# Revit family: Glulam-Southern Pine-Column
name_source: partatom
category: Structural Columns
revit_build: Autodesk Revit Architecture 2012 (Build: 20110210_1515)
units: mm (PartAtom-declared; Revit-internal decimal feet)

## types (160) — shared parameters
Assembly Code = B10

## per-type parameters (varying)
| type | A | Ix | Iy | Laminations | Sx | Sy | b | d |
| 3x5.5 | 16.5 in² | 41.59 | 12.38 | 4 | 15.13 | 8.25 | 0' - 3" | 0' - 5 1/2" |
| 3x6.875 | 20.63 in² | 81.24 | 15.47 | 5 | 23.63 | 10.31 | 0' - 3" | 0' - 6 7/8" |
| 3x8.25 | 24.75 in² | 140.4 | 18.56 | 6 | 34.03 | 12.38 | 0' - 3" | 0' - 8 1/4" |
| 3x9.625 | 28.88 in² | 222.9 | 21.66 | 7 | 46.32 | 14.44 | 0' - 3" | 0' - 9 5/8" |
| 3x11 | 33 in² | 332.8 | 24.75 | 8 | 60.5 | 16.5 | 0' - 3" | 0' - 11" |
| 3x12.375 | 37.13 in² | 473.8 | 27.84 | 9 | 76.57 | 18.56 | 0' - 3" | 1' - 0 3/8" |
| 3x13.75 | 41.25 in² | 649.9 | 30.94 | 10 | 94.53 | 20.63 | 0' - 3" | 1' - 1 3/4" |
| 3x15.125 | 45.38 in² | 865 | 34.03 | 11 | 114.4 | 22.69 | 0' - 3" | 1' - 3 1/8" |
| 3x16.5 | 49.5 in² | 1123 | 37.13 | 12 | 136.1 | 24.75 | 0' - 3" | 1' - 4 1/2" |
| 3x17.875 | 53.63 in² | 1428 | 40.22 | 13 | 159.8 | 26.81 | 0' - 3" | 1' - 5 7/8" |
| 3x19.25 | 57.75 in² | 1783 | 43.31 | 14 | 185.3 | 28.88 | 0' - 3" | 1' - 7 1/4" |
| 3x20.625 | 61.88 in² | 2193 | 46.41 | 15 | 212.7 | 30.94 | 0' - 3" | 1' - 8 5/8" |
| 3x22 | 66 in² | 2662 | 49.5 | 16 | 242 | 33 | 0' - 3" | 1' - 10" |
| 3x23.375 | 70.13 in² | 3193 | 52.59 | 17 | 273.2 | 35.06 | 0' - 3" | 1' - 11 3/8" |
| 3x24.75 | 74.25 in² | 3790 | 55.69 | 18 | 306.3 | 37.13 | 0' - 3" | 2' - 0 3/4" |
| 5x5.5 | 27.5 in² | 69.32 | 57.29 | 4 | 25.21 | 22.92 | 0' - 5" | 0' - 5 1/2" |
| 5x6.875 | 34.38 in² | 135.4 | 71.61 | 5 | 39.39 | 28.65 | 0' - 5" | 0' - 6 7/8" |
| 5x8.25 | 41.25 in² | 234 | 85.94 | 6 | 56.72 | 34.38 | 0' - 5" | 0' - 8 1/4" |
| 5x9.625 | 48.13 in² | 371.5 | 100.3 | 7 | 77.2 | 40.1 | 0' - 5" | 0' - 9 5/8" |
| 5x11 | 55 in² | 554.6 | 114.6 | 8 | 100.8 | 45.83 | 0' - 5" | 0' - 11" |
| 5x12.375 | 61.88 in² | 789.6 | 128.9 | 9 | 127.6 | 51.56 | 0' - 5" | 1' - 0 3/8" |
| 5x13.75 | 68.75 in² | 1083 | 143.2 | 10 | 157.6 | 57.29 | 0' - 5" | 1' - 1 3/4" |
| 5x15.125 | 75.63 in² | 1442 | 157.6 | 11 | 190.6 | 63.02 | 0' - 5" | 1' - 3 1/8" |
| 5x16.5 | 82.5 in² | 1872 | 171.9 | 12 | 226.9 | 68.75 | 0' - 5" | 1' - 4 1/2" |
| 5x17.875 | 89.38 in² | 2380 | 186.2 | 13 | 266.3 | 74.48 | 0' - 5" | 1' - 5 7/8" |
| 5x19.25 | 96.25 in² | 2972 | 200.5 | 14 | 308.8 | 80.21 | 0' - 5" | 1' - 7 1/4" |
| 5x20.625 | 103.1 in² | 3656 | 214.8 | 15 | 354.5 | 85.94 | 0' - 5" | 1' - 8 5/8" |
| 5x22 | 110 in² | 4437 | 229.2 | 16 | 403.3 | 91.67 | 0' - 5" | 1' - 10" |
| 5x23.375 | 116.9 in² | 5322 | 243.5 | 17 | 455.3 | 97.4 | 0' - 5" | 1' - 11 3/8" |
| 5x24.75 | 123.8 in² | 6317 | 257.8 | 18 | 510.5 | 103.1 | 0' - 5" | 2' - 0 3/4" |
| 5x26.125 | 130.6 in² | 7429 | 272.1 | 19 | 568.8 | 108.9 | 0' - 5" | 2' - 2 1/8" |
| 5x27.5 | 137.5 in² | 8665 | 286.5 | 20 | 630.2 | 114.6 | 0' - 5" | 2' - 3 1/2" |
| 5x28.875 | 144.4 in² | 10031 | 300.8 | 21 | 694.8 | 120.3 | 0' - 5" | 2' - 4 7/8" |
| 5x30.25 | 151.3 in² | 11534 | 315.1 | 22 | 762.6 | 126 | 0' - 5" | 2' - 6 1/4" |
| 5x31.625 | 158.1 in² | 13179 | 329.4 | 23 | 833.5 | 131.8 | 0' - 5" | 2' - 7 5/8" |
| 5x33 | 165 in² | 14974 | 343.8 | 24 | 907.5 | 137.5 | 0' - 5" | 2' - 9" |
| 5x34.375 | 171.9 in² | 16925 | 358.1 | 25 | 984.7 | 143.2 | 0' - 5" | 2' - 10 3/8" |
| 5x35.75 | 178.8 in² | 19038 | 372.4 | 26 | 1065 | 149 | 0' - 5" | 2' - 11 3/4" |
| 6.75x6.875 | 46.41 in² | 182.8 | 176.2 | 5 | 53.17 | 52.21 | 0' - 6 3/4" | 0' - 6 7/8" |
| 6.75x8.25 | 55.69 in² | 315.9 | 211.4 | 6 | 76.57 | 62.65 | 0' - 6 3/4" | 0' - 8 1/4" |
| 6.75x9.625 | 64.97 in² | 501.6 | 246.7 | 7 | 104.2 | 73.09 | 0' - 6 3/4" | 0' - 9 5/8" |
| 6.75x11 | 74.25 in² | 748.7 | 281.9 | 8 | 136.1 | 83.53 | 0' - 6 3/4" | 0' - 11" |
| 6.75x12.375 | 83.53 in² | 1066 | 317.2 | 9 | 172.3 | 93.97 | 0' - 6 3/4" | 1' - 0 3/8" |
| 6.75x13.75 | 92.81 in² | 1462 | 352.4 | 10 | 212.7 | 104.4 | 0' - 6 3/4" | 1' - 1 3/4" |
| 6.75x15.125 | 102.1 in² | 1946 | 387.6 | 11 | 257.4 | 114.9 | 0' - 6 3/4" | 1' - 3 1/8" |
| 6.75x16.5 | 111.4 in² | 2527 | 422.9 | 12 | 306.3 | 125.3 | 0' - 6 3/4" | 1' - 4 1/2" |
| 6.75x17.875 | 120.7 in² | 3213 | 458.1 | 13 | 359.5 | 135.7 | 0' - 6 3/4" | 1' - 5 7/8" |
| 6.75x19.25 | 129.9 in² | 4012 | 493.4 | 14 | 416.9 | 146.2 | 0' - 6 3/4" | 1' - 7 1/4" |
| 6.75x20.625 | 139.2 in² | 4935 | 528.6 | 15 | 478.6 | 156.6 | 0' - 6 3/4" | 1' - 8 5/8" |
| 6.75x22 | 148.5 in² | 5990 | 563.8 | 16 | 544.5 | 167.1 | 0' - 6 3/4" | 1' - 10" |
| 6.75x23.375 | 157.8 in² | 7184 | 599.1 | 17 | 614.7 | 177.5 | 0' - 6 3/4" | 1' - 11 3/8" |
| 6.75x24.75 | 167.1 in² | 8528 | 634.3 | 18 | 689.1 | 187.9 | 0' - 6 3/4" | 2' - 0 3/4" |
| 6.75x26.125 | 176.3 in² | 10030 | 669.6 | 19 | 767.8 | 198.4 | 0' - 6 3/4" | 2' - 2 1/8" |
| 6.75x27.5 | 185.6 in² | 11698 | 704.8 | 20 | 850.8 | 208.8 | 0' - 6 3/4" | 2' - 3 1/2" |
| 6.75x28.875 | 194.9 in² | 13542 | 740 | 21 | 938 | 219.3 | 0' - 6 3/4" | 2' - 4 7/8" |
| 6.75x30.25 | 204.2 in² | 15570 | 775.3 | 22 | 1029 | 229.7 | 0' - 6 3/4" | 2' - 6 1/4" |
| 6.75x31.625 | 213.5 in² | 17792 | 810.5 | 23 | 1125 | 240.2 | 0' - 6 3/4" | 2' - 7 5/8" |
| 6.75x33 | 222.8 in² | 20215 | 845.8 | 24 | 1225 | 250.6 | 0' - 6 3/4" | 2' - 9" |
| 6.75x34.375 | 232 in² | 22848 | 881 | 25 | 1329 | 261 | 0' - 6 3/4" | 2' - 10 3/8" |
| 6.75x35.75 | 241.3 in² | 25701 | 916.2 | 26 | 1438 | 271.5 | 0' - 6 3/4" | 2' - 11 3/4" |
| 6.75x37.125 | 250.6 in² | 28782 | 951.5 | 27 | 1551 | 281.9 | 0' - 6 3/4" | 3' - 1 1/8" |
| 6.75x38.5 | 259.9 in² | 32100 | 986.7 | 28 | 1668 | 292.4 | 0' - 6 3/4" | 3' - 2 1/2" |
| 6.75x39.875 | 269.2 in² | 35664 | 1022 | 29 | 1789 | 302.8 | 0' - 6 3/4" | 3' - 3 7/8" |
| 6.75x41.25 | 278.4 in² | 39482 | 1057 | 30 | 1914 | 313.2 | 0' - 6 3/4" | 3' - 5 1/4" |
| 6.75x42.625 | 287.7 in² | 43563 | 1092 | 31 | 2044 | 323.7 | 0' - 6 3/4" | 3' - 6 5/8" |
| 6.75x44 | 297 in² | 47916 | 1128 | 32 | 2178 | 334.1 | 0' - 6 3/4" | 3' - 8" |
| 6.75x45.375 | 306.3 in² | 52550 | 1163 | 33 | 2316 | 344.6 | 0' - 6 3/4" | 3' - 9 3/8" |
| 6.75x46.75 | 315.6 in² | 57473 | 1198 | 34 | 2459 | 355 | 0' - 6 3/4" | 3' - 10 3/4" |
| 6.75x48.125 | 324.8 in² | 62695 | 1233 | 35 | 2606 | 365.4 | 0' - 6 3/4" | 4' - 0 1/8" |
| 8.5x8.25 | 70.1 in² | 397.7 | 422.21 | 6 | 96.42 | 99.34 | 0' - 8 1/2" | 0' - 8 1/4" |
| 8.5x9.625 | 81.8 in² | 631.6 | 492.58 | 7 | 131.2 | 115.9 | 0' - 8 1/2" | 0' - 9 5/8" |
| 8.5x11 | 93.5 in² | 942.8 | 562.95 | 8 | 171.4 | 132.5 | 0' - 8 1/2" | 0' - 11" |
| 8.5x12.375 | 105.2 in² | 1342 | 633.32 | 9 | 216.9 | 149 | 0' - 8 1/2" | 1' - 0 3/8" |
| 8.5x13.75 | 116.9 in² | 1841 | 703.68 | 10 | 267.8 | 165.6 | 0' - 8 1/2" | 1' - 1 3/4" |
| 8.5x15.125 | 128.6 in² | 2451 | 774.05 | 11 | 324.1 | 182.1 | 0' - 8 1/2" | 1' - 3 1/8" |
| 8.5x16.5 | 140.3 in² | 3182 | 844.42 | 12 | 385.7 | 198.7 | 0' - 8 1/2" | 1' - 4 1/2" |
| 8.5x17.875 | 151.9 in² | 4046 | 914.79 | 13 | 452.6 | 215.2 | 0' - 8 1/2" | 1' - 5 7/8" |
| 8.5x19.25 | 163.6 in² | 5053 | 985.16 | 14 | 525 | 231.8 | 0' - 8 1/2" | 1' - 7 1/4" |
| 8.5x20.625 | 175.3 in² | 6215 | 1056 | 15 | 602.6 | 248.4 | 0' - 8 1/2" | 1' - 8 5/8" |
| 8.5x22 | 187 in² | 7542 | 1126 | 16 | 685.7 | 264.9 | 0' - 8 1/2" | 1' - 10" |
| 8.5x23.375 | 198.7 in² | 9047 | 1196 | 17 | 774.1 | 281.5 | 0' - 8 1/2" | 1' - 11 3/8" |
| 8.5x24.75 | 210.4 in² | 10739 | 1267 | 18 | 867.8 | 298 | 0' - 8 1/2" | 2' - 0 3/4" |
| 8.5x26.125 | 222.1 in² | 12630 | 1337 | 19 | 966.9 | 314.6 | 0' - 8 1/2" | 2' - 2 1/8" |
| 8.5x27.5 | 233.8 in² | 14731 | 1407 | 20 | 1071 | 331.1 | 0' - 8 1/2" | 2' - 3 1/2" |
| 8.5x28.875 | 245.4 in² | 17053 | 1478 | 21 | 1181 | 347.7 | 0' - 8 1/2" | 2' - 4 7/8" |
| 8.5x30.25 | 257.1 in² | 19607 | 1548 | 22 | 1296 | 364.3 | 0' - 8 1/2" | 2' - 6 1/4" |
| 8.5x31.625 | 268.8 in² | 22404 | 1618 | 23 | 1417 | 380.8 | 0' - 8 1/2" | 2' - 7 5/8" |
| 8.5x33 | 280.5 in² | 25455 | 1689 | 24 | 1543 | 397.4 | 0' - 8 1/2" | 2' - 9" |
| 8.5x34.375 | 292.2 in² | 28772 | 1759 | 25 | 1674 | 413.9 | 0' - 8 1/2" | 2' - 10 3/8" |
| 8.5x35.75 | 303.9 in² | 32364 | 1830 | 26 | 1811 | 430.5 | 0' - 8 1/2" | 2' - 11 3/4" |
| 8.5x37.125 | 315.6 in² | 36244 | 1900 | 27 | 1953 | 447 | 0' - 8 1/2" | 3' - 1 1/8" |
| 8.5x38.5 | 327.3 in² | 40422 | 1970 | 28 | 2100 | 463.6 | 0' - 8 1/2" | 3' - 2 1/2" |
| 8.5x39.875 | 338.9 in² | 44910 | 2041 | 29 | 2253 | 480.2 | 0' - 8 1/2" | 3' - 3 7/8" |
| 8.5x41.25 | 350.6 in² | 49718 | 2111 | 30 | 2411 | 496.7 | 0' - 8 1/2" | 3' - 5 1/4" |
| 8.5x42.625 | 362.3 in² | 54857 | 2181 | 31 | 2574 | 513.3 | 0' - 8 1/2" | 3' - 6 5/8" |
| 8.5x44 | 374 in² | 60339 | 2252 | 32 | 2743 | 529.8 | 0' - 8 1/2" | 3' - 8" |
| 8.5x45.375 | 385.7 in² | 66174 | 2322 | 33 | 2917 | 546.4 | 0' - 8 1/2" | 3' - 9 3/8" |
| 8.5x46.75 | 397.4 in² | 72374 | 2393 | 34 | 3096 | 562.9 | 0' - 8 1/2" | 3' - 10 3/4" |
| 8.5x48.125 | 409.1 in² | 78950 | 2463 | 35 | 3281 | 579.5 | 0' - 8 1/2" | 4' - 0 1/8" |
| 8.5x49.5 | 420.8 in² | 85912 | 2533 | 36 | 3471 | 596.1 | 0' - 8 1/2" | 4' - 1 1/2" |
| 8.5x50.875 | 432.4 in² | 93272 | 2604 | 37 | 3667 | 612.6 | 0' - 8 1/2" | 4' - 2 7/8" |
| 8.5x52.25 | 444.1 in² | 101041 | 2674 | 38 | 3868 | 629.2 | 0' - 8 1/2" | 4' - 4 1/4" |
| 8.5x53.625 | 455.8 in² | 109229 | 2744 | 39 | 4074 | 645.7 | 0' - 8 1/2" | 4' - 5 5/8" |
| 8.5x55 | 467.5 in² | 117849 | 2815 | 40 | 4285 | 662.3 | 0' - 8 1/2" | 4' - 7" |
| 8.5x56.375 | 479.2 in² | 126910 | 2885 | 41 | 4502 | 678.8 | 0' - 8 1/2" | 4' - 8 3/8" |
| 8.5x57.75 | 490.9 in² | 136425 | 2955 | 42 | 4725 | 695.4 | 0' - 8 1/2" | 4' - 9 3/4" |
| 8.5x59.125 | 502.6 in² | 146403 | 3026 | 43 | 4952 | 712 | 0' - 8 1/2" | 4' - 11 1/8" |
| 8.5x60.5 | 514.3 in² | 156857 | 3096 | 44 | 5185 | 728.5 | 0' - 8 1/2" | 5' - 0 1/2" |
| 8.5x61.875 | 525.9 in² | 167797 | 3167 | 45 | 5424 | 745.1 | 0' - 8 1/2" | 5' - 1 7/8" |
| 8.5x63.25 | 537.6 in² | 179234 | 3237 | 46 | 5667 | 761.6 | 0' - 8 1/2" | 5' - 3 1/4" |
| 10.5x9.625 | 101.1 in² | 780.2 | 928.5 | 7 | 162.1 | 176.9 | 0' - 10 1/2" | 0' - 9 5/8" |
| 10.5x11 | 115.5 in² | 1165 | 1061 | 8 | 211.8 | 202.1 | 0' - 10 1/2" | 0' - 11" |
| 10.5x12.375 | 129.9 in² | 1658 | 1194 | 9 | 268 | 227.4 | 0' - 10 1/2" | 1' - 0 3/8" |
| 10.5x13.75 | 144.4 in² | 2275 | 1326 | 10 | 330.9 | 252.7 | 0' - 10 1/2" | 1' - 1 3/4" |
| 10.5x15.125 | 158.8 in² | 3028 | 1459 | 11 | 400.3 | 277.9 | 0' - 10 1/2" | 1' - 3 1/8" |
| 10.5x16.5 | 173.3 in² | 3931 | 1592 | 12 | 476.4 | 303.2 | 0' - 10 1/2" | 1' - 4 1/2" |
| 10.5x17.875 | 187.7 in² | 4997 | 1724 | 13 | 559.2 | 328.5 | 0' - 10 1/2" | 1' - 5 7/8" |
| 10.5x19.25 | 202.1 in² | 6242 | 1857 | 14 | 648.5 | 353.7 | 0' - 10 1/2" | 1' - 7 1/4" |
| 10.5x20.625 | 216.6 in² | 7677 | 1990 | 15 | 744.4 | 379 | 0' - 10 1/2" | 1' - 8 5/8" |
| 10.5x22 | 231 in² | 9317 | 2122 | 16 | 847 | 404.3 | 0' - 10 1/2" | 1' - 10" |
| 10.5x23.375 | 245.4 in² | 11175 | 2255 | 17 | 956.2 | 429.5 | 0' - 10 1/2" | 1' - 11 3/8" |
| 10.5x24.75 | 259.9 in² | 13266 | 2388 | 18 | 1072 | 454.8 | 0' - 10 1/2" | 2' - 0 3/4" |
| 10.5x26.125 | 274.3 in² | 15602 | 2520 | 19 | 1194 | 480 | 0' - 10 1/2" | 2' - 2 1/8" |
| 10.5x27.5 | 288.8 in² | 18197 | 2653 | 20 | 1323 | 505.3 | 0' - 10 1/2" | 2' - 3 1/2" |
| 10.5x28.875 | 303.2 in² | 21066 | 2786 | 21 | 1459 | 530.6 | 0' - 10 1/2" | 2' - 4 7/8" |
| 10.5x30.25 | 317.6 in² | 24221 | 2918 | 22 | 1601 | 555.8 | 0' - 10 1/2" | 2' - 6 1/4" |
| 10.5x31.625 | 332.1 in² | 27676 | 3051 | 23 | 1750 | 581.1 | 0' - 10 1/2" | 2' - 7 5/8" |
| 10.5x33 | 346.5 in² | 31445 | 3183 | 24 | 1906 | 606.4 | 0' - 10 1/2" | 2' - 9" |
| 10.5x34.375 | 360.9 in² | 35542 | 3316 | 25 | 2068 | 631.6 | 0' - 10 1/2" | 2' - 10 3/8" |
| 10.5x35.75 | 375.4 in² | 39979 | 3449 | 26 | 2237 | 656.9 | 0' - 10 1/2" | 2' - 11 3/4" |
| 10.5x37.125 | 389.8 in² | 44772 | 3581 | 27 | 2412 | 682.2 | 0' - 10 1/2" | 3' - 1 1/8" |
| 10.5x38.5 | 404.3 in² | 49933 | 3714 | 28 | 2594 | 707.4 | 0' - 10 1/2" | 3' - 2 1/2" |
| 10.5x39.875 | 418.7 in² | 55477 | 3847 | 29 | 2783 | 732.7 | 0' - 10 1/2" | 3' - 3 7/8" |
| 10.5x41.25 | 433.1 in² | 61416 | 3979 | 30 | 2978 | 758 | 0' - 10 1/2" | 3' - 5 1/4" |
| 10.5x42.625 | 447.6 in² | 67764 | 4112 | 31 | 3180 | 783.2 | 0' - 10 1/2" | 3' - 6 5/8" |
| 10.5x44 | 462 in² | 74536 | 4245 | 32 | 3388 | 808.5 | 0' - 10 1/2" | 3' - 8" |
| 10.5x45.375 | 476.4 in² | 81744 | 4377 | 33 | 3603 | 833.8 | 0' - 10 1/2" | 3' - 9 3/8" |
| 10.5x46.75 | 490.9 in² | 89403 | 4510 | 34 | 3825 | 859 | 0' - 10 1/2" | 3' - 10 3/4" |
| 10.5x48.125 | 505.3 in² | 97526 | 4643 | 35 | 4053 | 884.3 | 0' - 10 1/2" | 4' - 0 1/8" |
| 10.5x49.5 | 519.8 in² | 106126 | 4775 | 36 | 4288 | 909.6 | 0' - 10 1/2" | 4' - 1 1/2" |
| 10.5x50.875 | 534.2 in² | 115218 | 4908 | 37 | 4529 | 934.8 | 0' - 10 1/2" | 4' - 2 7/8" |
| 10.5x52.25 | 548.6 in² | 124815 | 5040 | 38 | 4778 | 960.1 | 0' - 10 1/2" | 4' - 4 1/4" |
| 10.5x53.625 | 563.1 in² | 134930 | 5173 | 39 | 5032 | 985.4 | 0' - 10 1/2" | 4' - 5 5/8" |
| 10.5x55 | 577.5 in² | 145578 | 5306 | 40 | 5294 | 1011 | 0' - 10 1/2" | 4' - 7" |
| 10.5x56.375 | 591.9 in² | 156772 | 5438 | 41 | 5562 | 1036 | 0' - 10 1/2" | 4' - 8 3/8" |
| 10.5x57.75 | 606.4 in² | 168525 | 5571 | 42 | 5836 | 1061 | 0' - 10 1/2" | 4' - 9 3/4" |
| 10.5x59.125 | 620.8 in² | 180851 | 5704 | 43 | 6118 | 1086 | 0' - 10 1/2" | 4' - 11 1/8" |
| 10.5x60.5 | 635.3 in² | 193764 | 5836 | 44 | 6405 | 1112 | 0' - 10 1/2" | 5' - 0 1/2" |
| 10.5x61.875 | 649.7 in² | 207278 | 5969 | 45 | 6700 | 1137 | 0' - 10 1/2" | 5' - 1 7/8" |
| 10.5x63.25 | 664.1 in² | 221406 | 6102 | 46 | 7001 | 1162 | 0' - 10 1/2" | 5' - 3 1/4" |
| 10.5x64.625 | 678.6 in² | 236162 | 6234 | 47 | 7309 | 1187 | 0' - 10 1/2" | 5' - 4 5/8" |
| 10.5x66 | 693 in² | 251559 | 6367 | 48 | 7623 | 1213 | 0' - 10 1/2" | 5' - 6" |
| 10.5x67.375 | 707.4 in² | 267611 | 6500 | 49 | 7944 | 1238 | 0' - 10 1/2" | 5' - 7 3/8" |
| 10.5x68.75 | 721.9 in² | 284332 | 6632 | 50 | 8271 | 1263 | 0' - 10 1/2" | 5' - 8 3/4" |
| 10.5x70.125 | 736.3 in² | 301736 | 6765 | 51 | 8606 | 1289 | 0' - 10 1/2" | 5' - 10 1/8" |
| 10.5x71.5 | 750.8 in² | 319835 | 6898 | 52 | 8946 | 1314 | 0' - 10 1/2" | 5' - 11 1/2" |
| 10.5x72.875 | 765.2 in² | 338644 | 7030 | 53 | 9294 | 1339 | 0' - 10 1/2" | 6' - 0 7/8" |
| 10.5x74.25 | 779.6 in² | 358177 | 7163 | 54 | 9648 | 1364 | 0' - 10 1/2" | 6' - 2 1/4" |
| 10.5x75.625 | 794.1 in² | 378446 | 7295 | 55 | 10008 | 1390 | 0' - 10 1/2" | 6' - 3 5/8" |
| 10.5x77 | 808.5 in² | 399466 | 7428 | 56 | 10376 | 1415 | 0' - 10 1/2" | 6' - 5" |

## geometry (parser evidence)
native form markers: Sweep x1
no freeform markers — native parametric forms only
